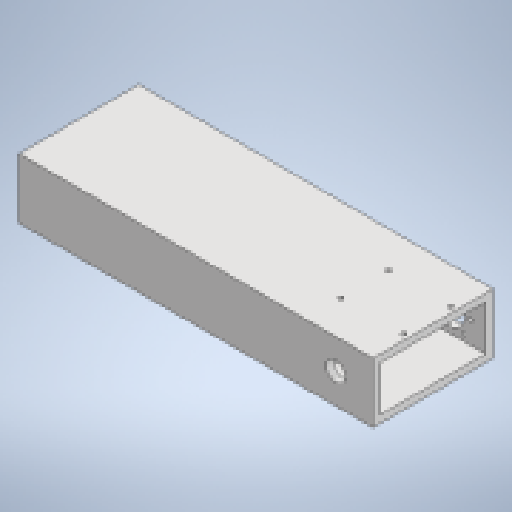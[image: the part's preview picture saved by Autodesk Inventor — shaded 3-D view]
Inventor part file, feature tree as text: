
AUTODESK INVENTOR PART (.ipt)
format: ipt  version: 2023 (Build 270158000, 158)  size: 177,152 bytes
history: native  units: in
note: dims shown in document units (in); Inventor stores cm internally (conversion verified against a paired STEP export)
features: extrude x5, sketch x5, shell x1
ambient origin geometry x8: Origin, YZ Plane, XZ Plane, XY Plane, X Axis, Y Axis, Z Axis, Center Point
bodies: Solid1 (feature_tree)
feature tree (11):
  extrude  "Extrusion1"  Depth=2.0in
  shell  "Shell1"  Thickness=11.811in
  extrude  "Extrusion2"  Depth=0.25in
  extrude  "Extrusion3"  Depth=1.5748in
  extrude  "Extrusion4"  Depth=11.811in TaperAngle=0.0deg
  extrude  "Extrusion5"  Depth=0.3937in
  sketch  "Sketch1"  dims[d0=4.0in d1=2.0in d2=11.811in d3=0.0in]
  sketch  "Sketch2"  dims[d4=0.25in d5=0.1575in]
  sketch  "Sketch3"  dims[d6=2.4803in d7=1.5748in]
  sketch  "Sketch4"  dims[d8=2.0866in d9=11.811in d10=0.0in]
  sketch  "Sketch5"  dims[d11=1.4961in d12=0.1575in d13=45.0deg d14=1.1024in d15=0.3937in d16=0.0in d17=0.6496in d18=0.3937in d19=0.0in d20=0.3937in d22=0.3937in d23=0.0in]
